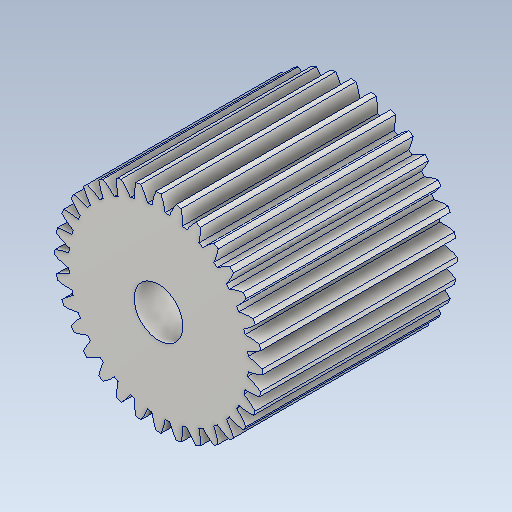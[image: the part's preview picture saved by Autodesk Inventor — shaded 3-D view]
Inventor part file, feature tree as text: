
AUTODESK INVENTOR PART (.ipt)
format: ipt  version: 2021 (Build 250183000, 183)  size: 383,488 bytes
history: native  units: mm
features: other x13, sketch x3, plane x2
ambient origin geometry x8: Origin, YZ Plane, XZ Plane, XY Plane, X Axis, Y Axis, Z Axis, Center Point
bodies: Solid1 (feature_tree)
feature tree (18):
  other  "Spur Gear1"
  other  "Solid1::Spur Gear1"
  other  "TaggingFeature1"
  sketch  "Sketch1"  dims[d0=10.0mm]
  sketch  "Sketch2"  dims[d16=80.0mm d17=0.0mm d41=0.0mm d43=80.0mm d46=80.0mm d47=0.0mm d48=0.0mm]
  sketch  "Sketch3"
  plane  "XZ Plane_1"
  plane  "Work Plane2"
  other  "Z Axis_1"
  other  "Srf1"
  other  "Srf1::Derived"
  other  "Distance iMate"
  other  "Align iMate"
  other  "Mesh iMate"
  other  "Axis iMate"
  other  "Position iMate"
  other  "Mesh iMate2"
  other  "Start plane iMate"
